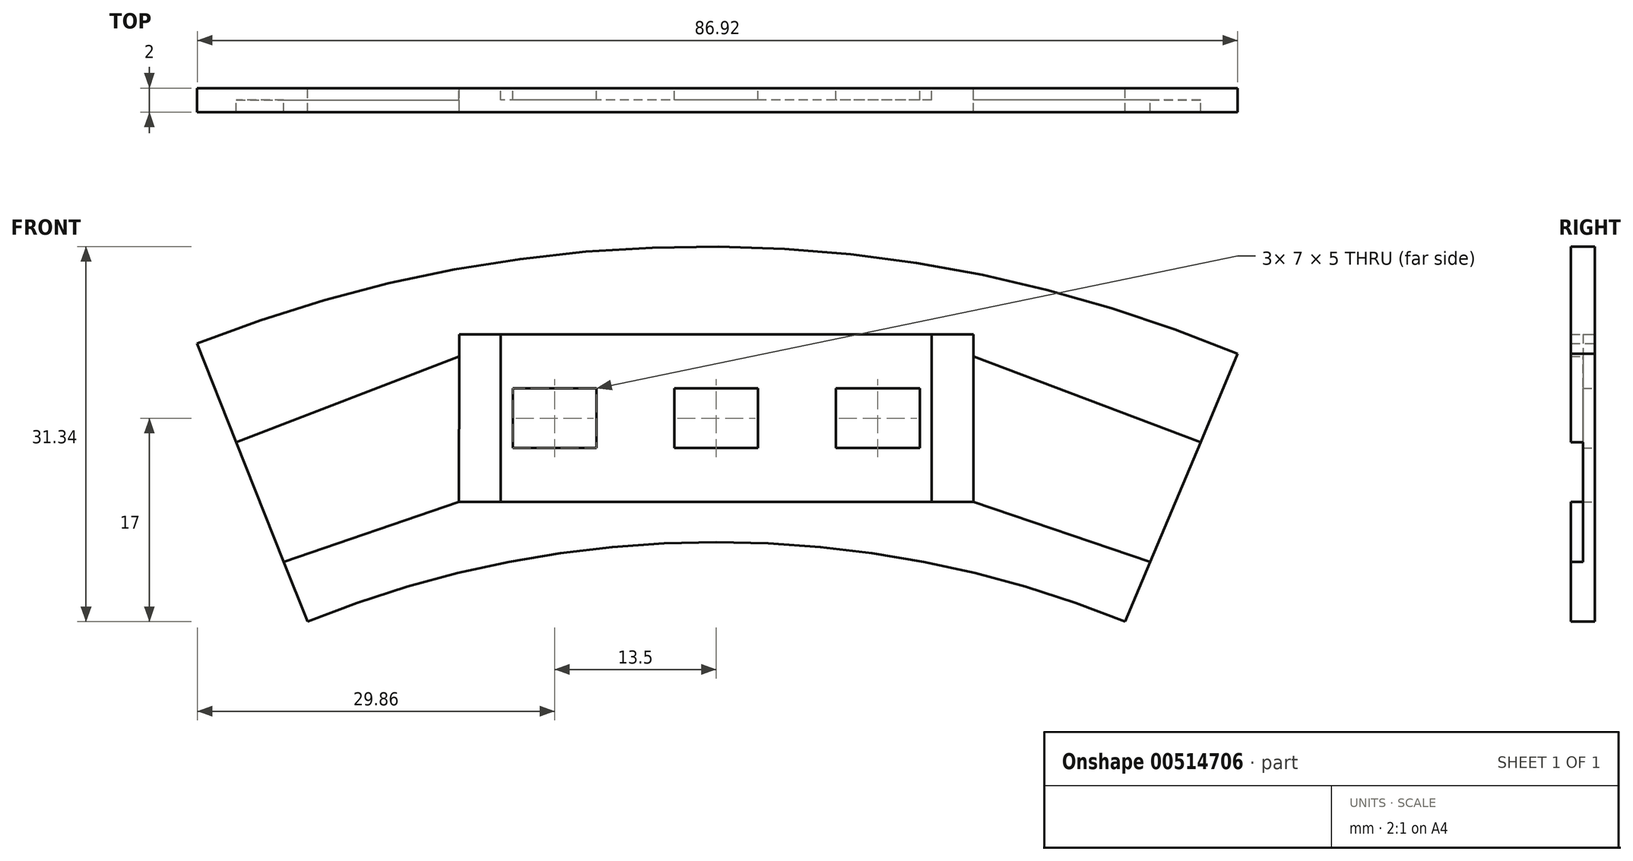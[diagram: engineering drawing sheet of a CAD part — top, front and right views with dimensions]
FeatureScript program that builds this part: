
annotation { "Feature Type Name" : "Feature", "Feature Type Description" : "" }
export const myFeature = defineFeature(function(context is Context, id is Id, definition is map)
    precondition{}
    {
        {
            var Q0;
            Q0=qCreatedBy(makeId("Front.planeOp"),FACE);
            var sketch = newSketch(context, id + "F0", { "sketchPlane" : qUnion([Q0])});
            skArc(sketch, "E0", {"start": v(43.56, 7.37) * mm, "mid": v(0.18, 16.33) * mm, "end": v(-43.36, 8.24) * mm});
            skLineSegment(sketch, "E1", {"start": v(34.16, -15) * mm, "end": v(43.56, 7.37) * mm});
            skLineSegment(sketch, "E2", {"start": v(-34.14, -15) * mm, "end": v(-43.36, 8.24) * mm});
            skLineSegment(sketch, "E3.bottom", {"start": v(21.5, -5) * mm, "end": v(-21.5, -5) * mm});
            skLineSegment(sketch, "E3.top", {"start": v(21.5, 9) * mm, "end": v(-21.5, 9) * mm});
            skLineSegment(sketch, "E3.left", {"start": v(21.5, -5) * mm, "end": v(21.5, 9) * mm});
            skLineSegment(sketch, "E3.right", {"start": v(-21.5, -5) * mm, "end": v(-21.48, 9) * mm});
            skPoint(sketch, "E3.middle", {"position": v(0, 2) * mm});
            skLineSegment(sketch, "E4.bottom", {"start": v(3.5, -0.5) * mm, "end": v(-3.5, -0.5) * mm});
            skLineSegment(sketch, "E4.top", {"start": v(3.5, 4.5) * mm, "end": v(-3.5, 4.5) * mm});
            skLineSegment(sketch, "E4.left", {"start": v(3.5, -0.5) * mm, "end": v(3.5, 4.5) * mm});
            skLineSegment(sketch, "E4.right", {"start": v(-3.5, -0.5) * mm, "end": v(-3.5, 4.5) * mm});
            skLineSegment(sketch, "E5.1.0.0", {"start": v(17, -0.5) * mm, "end": v(10, -0.5) * mm});
            skLineSegment(sketch, "E5.1.0.1", {"start": v(17, 4.5) * mm, "end": v(10, 4.5) * mm});
            skLineSegment(sketch, "E5.1.0.2", {"start": v(10, -0.5) * mm, "end": v(10, 4.5) * mm});
            skPoint(sketch, "E5.1.0.3", {"position": v(13.5, 2) * mm});
            skLineSegment(sketch, "E5.1.0.4", {"start": v(17, -0.5) * mm, "end": v(17, 4.5) * mm});
            skPoint(sketch, "E5.1.0.5", {"position": v(13.5, 2) * mm});
            skLineSegment(sketch, "E5.direction1", {"start": v(-3.5, -0.5) * mm, "end": v(10, -0.5) * mm, "construction": true});
            skLineSegment(sketch, "E6.1.0.1", {"start": v(10, -0.5) * mm, "end": v(10, 2.5) * mm});
            skLineSegment(sketch, "E6.1.0.3", {"start": v(15, -0.5) * mm, "end": v(10, -0.5) * mm});
            skLineSegment(sketch, "E7.1.0.0", {"start": v(-10, -0.5) * mm, "end": v(-10, 4.5) * mm});
            skLineSegment(sketch, "E7.1.0.1", {"start": v(-17, -0.5) * mm, "end": v(-17, 4.5) * mm});
            skLineSegment(sketch, "E7.1.0.2", {"start": v(-10, -0.5) * mm, "end": v(-17, -0.5) * mm});
            skPoint(sketch, "E7.1.0.3", {"position": v(-13.5, 2) * mm});
            skLineSegment(sketch, "E7.1.0.4", {"start": v(-10, 4.5) * mm, "end": v(-17, 4.5) * mm});
            skPoint(sketch, "E7.1.0.5", {"position": v(-13.5, 2) * mm});
            skLineSegment(sketch, "E7.direction1", {"start": v(-3.5, -0.5) * mm, "end": v(-17, -0.5) * mm, "construction": true});
            skArc(sketch, "E8.trimOffspring", {"start": v(34.16, -15) * mm, "mid": v(0, -8.27) * mm, "end": v(-34.14, -15) * mm, "construction": true});
            skArc(sketch, "E9.trimOffspring", {"start": v(34.16, -15) * mm, "mid": v(0, -8.36) * mm, "end": v(-34.15, -15) * mm});
            skLineSegment(sketch, "E10", {"start": v(-36.13, -10) * mm, "end": v(-21.5, -5) * mm});
            skLineSegment(sketch, "E11", {"start": v(-40.1, 0) * mm, "end": v(-21.48, 7.16) * mm});
            skLineSegment(sketch, "E12", {"start": v(36.26, -10) * mm, "end": v(21.5, -5) * mm});
            skLineSegment(sketch, "E13", {"start": v(40.46, 0) * mm, "end": v(21.5, 7.16) * mm});
            skLineSegment(sketch, "E14", {"start": v(-18, 9) * mm, "end": v(-18, -5) * mm});
            skLineSegment(sketch, "E15", {"start": v(18, 9) * mm, "end": v(18, -5) * mm});
            skSolve(sketch);
        }
        {
            var Q0;
            Q0=makeQuery(id+"F0.imprint","IMPRINT",FACE,{"disambiguationData":[TD([[makeQuery(id+"F0.imprint","IMPRINT",EDGE,{"derivedFrom":sQuery(id+"F0.wireOp",EDGE,"E0")}),1.0]])]});
            extrude(context, id + "F1", {"entities" : qUnion([Q0]), "depth" : 2 * mm, "offsetDistance" : 25 * mm});
        }
        {
            var Q0;
            Q0=makeQuery(id+"F0.imprint","IMPRINT",FACE,{"disambiguationData":[TD([[makeQuery(id+"F0.imprint","IMPRINT",EDGE,{"derivedFrom":sQuery(id+"F0.wireOp",EDGE,"E3.bottom")}),-1.0]])]});
            extrude(context, id + "F2", {"entities" : qUnion([Q0]), "operationType" : NewBodyOperationType.ADD, "depth" : 1 * mm, "offsetDistance" : 25 * mm});
        }
        {
            var Q0;
            Q0=makeQuery(id+"F0.imprint","IMPRINT",FACE,{"disambiguationData":[TD([[makeQuery(id+"F0.imprint","IMPRINT",EDGE,{"derivedFrom":sQuery(id+"F0.wireOp",EDGE,"E3.bottom")}),1.0]])]});
            extrude(context, id + "F3", {"entities" : qUnion([Q0]), "operationType" : NewBodyOperationType.ADD, "depth" : 2 * mm, "offsetDistance" : 25 * mm});
        }
        {
            var Q0;
            {var subQ0=sQuery(id+"F0.wireOp",EDGE,"E12");Q0=makeQuery(id+"F0.imprint","IMPRINT",FACE,{"disambiguationData":[TD([[makeQuery(id+"F0.imprint","IMPRINT",EDGE,{"derivedFrom":subQ0}),-1.0]])]});}
            extrude(context, id + "F4", {"entities" : qUnion([Q0]), "operationType" : NewBodyOperationType.ADD, "depth" : 1 * mm, "offsetDistance" : 25 * mm});
        }
        {
            var Q0;
            {var subQ0=sQuery(id+"F0.wireOp",EDGE,"E10");Q0=makeQuery(id+"F0.imprint","IMPRINT",FACE,{"disambiguationData":[TD([[makeQuery(id+"F0.imprint","IMPRINT",EDGE,{"derivedFrom":subQ0}),1.0]])]});}
            extrude(context, id + "F5", {"entities" : qUnion([Q0]), "operationType" : NewBodyOperationType.ADD, "depth" : 1 * mm, "offsetDistance" : 25 * mm});
        }
        {
            var Q0;
            {var subQ6=sQuery(id+"F0.wireOp",EDGE,"E15");Q0=makeQuery(id+"F0.imprint","IMPRINT",FACE,{"disambiguationData":[TD([[makeQuery(id+"F0.imprint","IMPRINT",EDGE,{"derivedFrom":subQ6}),1.0]])]});}
            extrude(context, id + "F6", {"entities" : qUnion([Q0]), "operationType" : NewBodyOperationType.REMOVE, "endBound" : BoundingType.THROUGH_ALL, "depth" : 0.5 * mm, "offsetDistance" : 25 * mm});
        }
        {
            var Q0;
            {var subQ6=sQuery(id+"F0.wireOp",EDGE,"E14");Q0=makeQuery(id+"F0.imprint","IMPRINT",FACE,{"disambiguationData":[TD([[makeQuery(id+"F0.imprint","IMPRINT",EDGE,{"derivedFrom":subQ6}),-1.0]])]});}
            extrude(context, id + "F7", {"entities" : qUnion([Q0]), "operationType" : NewBodyOperationType.REMOVE, "endBound" : BoundingType.THROUGH_ALL, "depth" : 25 * mm, "offsetDistance" : 25 * mm});
        }
        {
            var Q0;
            Q0=makeQuery(id+"F0.imprint","IMPRINT",FACE,{"disambiguationData":[TD([[makeQuery(id+"F0.imprint","IMPRINT",EDGE,{"derivedFrom":sQuery(id+"F0.wireOp",EDGE,"E4.bottom")}),1.0]])]});
            extrude(context, id + "F8", {"entities" : qUnion([Q0]), "operationType" : NewBodyOperationType.ADD, "depth" : 1 * mm, "offsetDistance" : 25 * mm});
        }
    });
